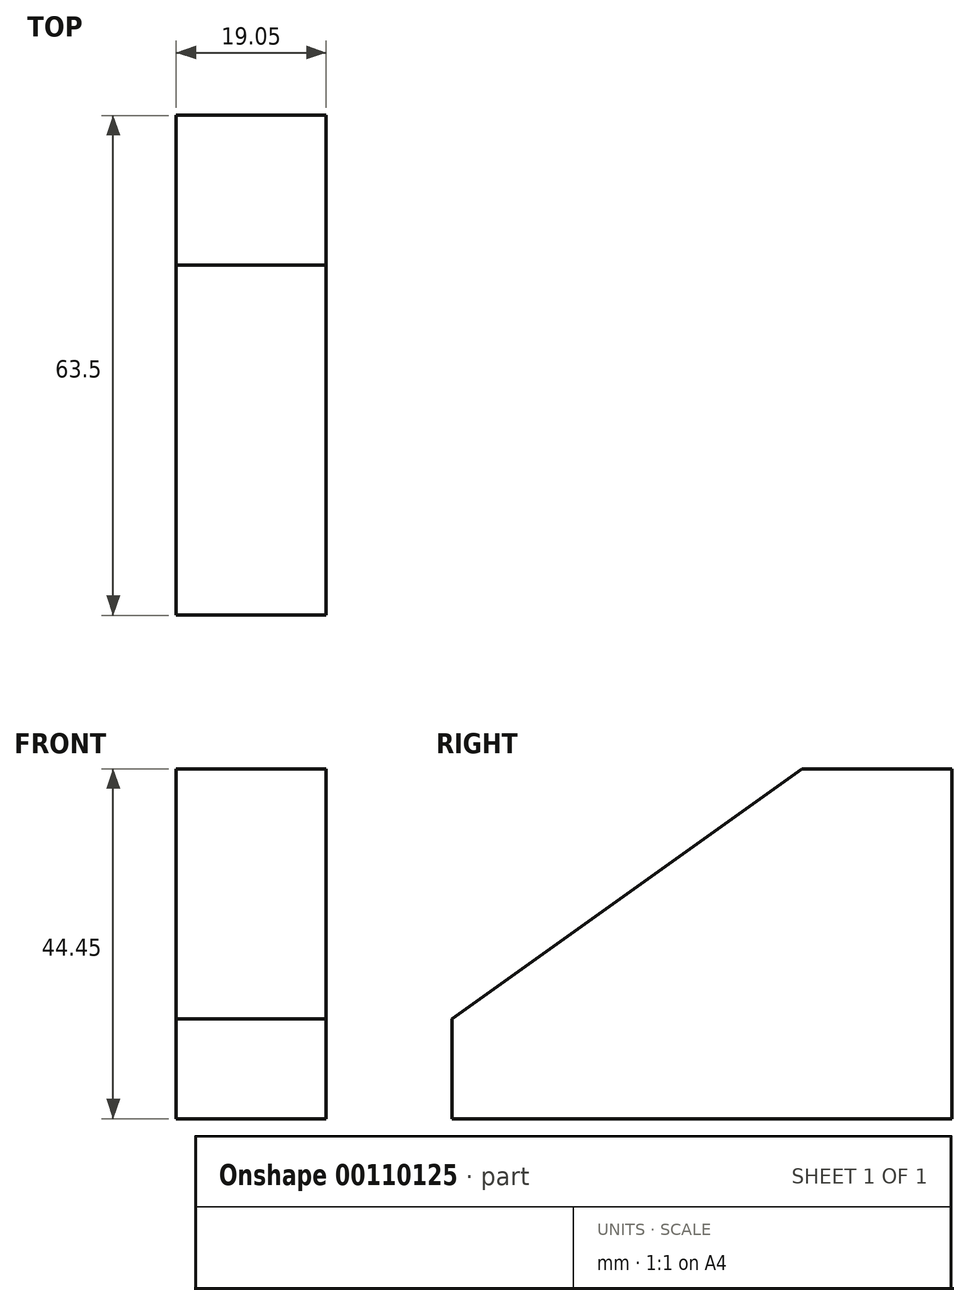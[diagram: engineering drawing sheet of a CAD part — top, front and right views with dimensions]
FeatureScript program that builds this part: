
annotation { "Feature Type Name" : "Feature", "Feature Type Description" : "" }
export const myFeature = defineFeature(function(context is Context, id is Id, definition is map)
    precondition{}
    {
        {
            var Q0;
            Q0=qCreatedBy(makeId("Right.planeOp"),FACE);
            var sketch = newSketch(context, id + "F0", { "sketchPlane" : qUnion([Q0])});
            skLineSegment(sketch, "E0", {"start": v(-33.97, -25.36) * mm, "end": v(29.53, -25.36) * mm});
            skLineSegment(sketch, "E1", {"start": v(29.53, -25.36) * mm, "end": v(29.53, 19.1) * mm});
            skLineSegment(sketch, "E2", {"start": v(29.53, 19.1) * mm, "end": v(10.48, 19.1) * mm});
            skLineSegment(sketch, "E3", {"start": v(-33.97, -25.36) * mm, "end": v(-33.97, -12.66) * mm});
            skLineSegment(sketch, "E4", {"start": v(10.48, 19.1) * mm, "end": v(-33.97, -12.66) * mm});
            skSolve(sketch);
        }
        {
            var Q0;
            Q0=makeQuery(id+"F0.imprint","IMPRINT",FACE,{"disambiguationData":[TD([[makeQuery(id+"F0.imprint","IMPRINT",EDGE,{"derivedFrom":sQuery(id+"F0.wireOp",EDGE,"E0")}),1.0]])]});
            extrude(context, id + "F1", {"entities" : qUnion([Q0]), "oppositeDirection" : true, "depth" : 19.05 * mm});
        }
    });
